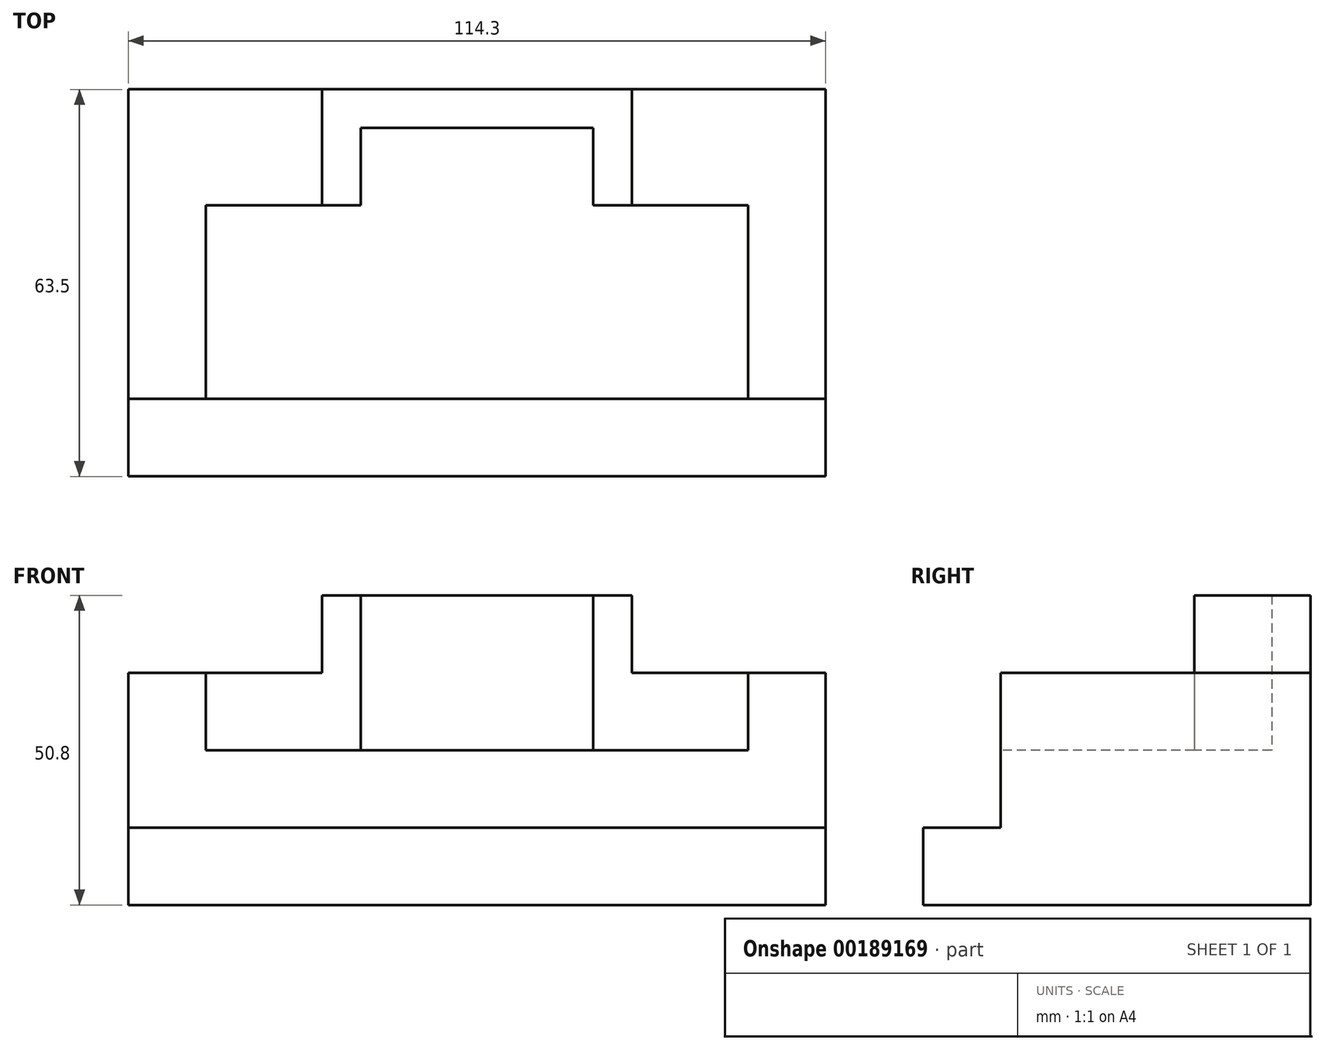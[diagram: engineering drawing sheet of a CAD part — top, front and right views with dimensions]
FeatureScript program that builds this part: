
annotation { "Feature Type Name" : "Feature", "Feature Type Description" : "" }
export const myFeature = defineFeature(function(context is Context, id is Id, definition is map)
    precondition{}
    {
        {
            var Q0;
            Q0=qCreatedBy(makeId("Right.planeOp"),FACE);
            var sketch = newSketch(context, id + "F0", { "sketchPlane" : qUnion([Q0])});
            skLineSegment(sketch, "E0", {"start": v(-32.34, 0) * mm, "end": v(31.16, 0) * mm});
            skLineSegment(sketch, "E1", {"start": v(31.16, 0) * mm, "end": v(31.16, 25.4) * mm});
            skLineSegment(sketch, "E2", {"start": v(31.16, 25.4) * mm, "end": v(-19.64, 25.4) * mm});
            skLineSegment(sketch, "E3", {"start": v(-19.64, 25.4) * mm, "end": v(-19.64, 12.7) * mm});
            skLineSegment(sketch, "E4", {"start": v(-19.64, 12.7) * mm, "end": v(-32.34, 12.7) * mm});
            skLineSegment(sketch, "E5", {"start": v(-32.34, 12.7) * mm, "end": v(-32.34, 0) * mm});
            skSolve(sketch);
        }
        {
            var Q0;
            Q0=makeQuery(id+"F0.imprint","IMPRINT",FACE,{"disambiguationData":[TD([[makeQuery(id+"F0.imprint","IMPRINT",EDGE,{"derivedFrom":sQuery(id+"F0.wireOp",EDGE,"E0")}),1.0]])]});
            extrude(context, id + "F1", {"entities" : qUnion([Q0]), "depth" : 114.3 * mm});
        }
        {
            var Q0;
            Q0=makeQuery(id+"F1.opExtrude","SWEPT_FACE",FACE,{"disambiguationData":[OSD([sQuery(id+"F0.wireOp",EDGE,"E2")])]});
            cPlane(context, id + "F2", {"entities" : qUnion([Q0]), "cplaneType" : CPlaneType.OFFSET, "offset" : 0 * mm, "width" : 152.4 * mm, "height" : 152.4 * mm});
        }
        {
            var Q0;
            Q0=qCreatedBy(id+"F2.planeOp",FACE);
            var sketch = newSketch(context, id + "F3", { "sketchPlane" : qUnion([Q0])});
            skLineSegment(sketch, "E6.0", {"start": v(114.3, 31.16) * mm, "end": v(0, 31.16) * mm});
            skLineSegment(sketch, "E7.0", {"start": v(0, 31.16) * mm, "end": v(0, -19.64) * mm});
            skLineSegment(sketch, "E8.0", {"start": v(114.3, -19.64) * mm, "end": v(0, -19.64) * mm});
            skLineSegment(sketch, "E9.0", {"start": v(114.3, 31.16) * mm, "end": v(114.3, -19.64) * mm});
            skLineSegment(sketch, "E10", {"start": v(0, -19.64) * mm, "end": v(0, 31.16) * mm});
            skLineSegment(sketch, "E11", {"start": v(0, -19.64) * mm, "end": v(12.7, -19.64) * mm});
            skLineSegment(sketch, "E12", {"start": v(12.7, -19.64) * mm, "end": v(12.7, 12.11) * mm});
            skLineSegment(sketch, "E13", {"start": v(12.7, 12.11) * mm, "end": v(38.1, 12.11) * mm});
            skLineSegment(sketch, "E14", {"start": v(38.1, 12.11) * mm, "end": v(38.1, 24.81) * mm});
            skLineSegment(sketch, "E15", {"start": v(38.1, 24.81) * mm, "end": v(76.2, 24.81) * mm});
            skLineSegment(sketch, "E16", {"start": v(76.2, 24.81) * mm, "end": v(76.2, 12.11) * mm});
            skLineSegment(sketch, "E17", {"start": v(76.2, 12.11) * mm, "end": v(101.6, 12.11) * mm});
            skLineSegment(sketch, "E18", {"start": v(101.6, 12.11) * mm, "end": v(101.6, -19.64) * mm});
            skLineSegment(sketch, "E19", {"start": v(101.6, -19.64) * mm, "end": v(114.3, -19.64) * mm});
            skLineSegment(sketch, "E20", {"start": v(114.3, -19.64) * mm, "end": v(114.3, 31.16) * mm});
            skSolve(sketch);
        }
        {
            var Q0;
            Q0=makeQuery(id+"F3.imprint","IMPRINT",FACE,{"disambiguationData":[TD([[makeQuery(id+"F3.imprint","IMPRINT",EDGE,{"derivedFrom":sQuery(id+"F3.wireOp",EDGE,"E6.0")}),1.0]])]});
            extrude(context, id + "F4", {"entities" : qUnion([Q0]), "operationType" : NewBodyOperationType.ADD, "depth" : 12.7 * mm});
        }
        {
            var Q0;
            Q0=makeQuery(id+"F4.opExtrude","CAP_FACE",FACE,{"disambiguationData":[OSD([sQuery(id+"F3.wireOp",EDGE,"E6.0"),sQuery(id+"F3.wireOp",EDGE,"E11"),sQuery(id+"F3.wireOp",EDGE,"E12"),sQuery(id+"F3.wireOp",EDGE,"E13"),sQuery(id+"F3.wireOp",EDGE,"E14"),sQuery(id+"F3.wireOp",EDGE,"E15"),sQuery(id+"F3.wireOp",EDGE,"E16"),sQuery(id+"F3.wireOp",EDGE,"E17"),sQuery(id+"F3.wireOp",EDGE,"E18"),sQuery(id+"F3.wireOp",EDGE,"E19"),sQuery(id+"F3.wireOp",EDGE,"E20"),sQuery(id+"F3.wireOp",EDGE,"E7.0")])],"isStart":false});
            var sketch = newSketch(context, id + "F5", { "sketchPlane" : qUnion([Q0])});
            skLineSegment(sketch, "E21.0.0", {"start": v(114.3, -19.64) * mm, "end": v(114.3, 31.16) * mm});
            skLineSegment(sketch, "E21.0.1", {"start": v(114.3, 31.16) * mm, "end": v(0, 31.16) * mm});
            skLineSegment(sketch, "E21.0.2", {"start": v(0, 31.16) * mm, "end": v(0, -19.64) * mm});
            skLineSegment(sketch, "E21.0.3", {"start": v(0, -19.64) * mm, "end": v(12.7, -19.64) * mm});
            skLineSegment(sketch, "E21.0.4", {"start": v(12.7, -19.64) * mm, "end": v(12.7, 12.11) * mm});
            skLineSegment(sketch, "E21.0.5", {"start": v(12.7, 12.11) * mm, "end": v(38.1, 12.11) * mm});
            skLineSegment(sketch, "E21.0.6", {"start": v(38.1, 12.11) * mm, "end": v(38.1, 24.81) * mm});
            skLineSegment(sketch, "E21.0.7", {"start": v(38.1, 24.81) * mm, "end": v(76.2, 24.81) * mm});
            skLineSegment(sketch, "E21.0.8", {"start": v(76.2, 24.81) * mm, "end": v(76.2, 12.11) * mm});
            skLineSegment(sketch, "E21.0.9", {"start": v(76.2, 12.11) * mm, "end": v(101.6, 12.11) * mm});
            skLineSegment(sketch, "E21.0.10", {"start": v(101.6, 12.11) * mm, "end": v(101.6, -19.64) * mm});
            skLineSegment(sketch, "E21.0.11", {"start": v(101.6, -19.64) * mm, "end": v(114.3, -19.64) * mm});
            skLineSegment(sketch, "E22", {"start": v(31.75, 31.16) * mm, "end": v(31.75, 12.11) * mm});
            skLineSegment(sketch, "E23", {"start": v(31.75, 12.11) * mm, "end": v(38.1, 12.11) * mm});
            skLineSegment(sketch, "E24", {"start": v(76.2, 12.11) * mm, "end": v(82.55, 12.11) * mm});
            skLineSegment(sketch, "E25", {"start": v(82.55, 12.11) * mm, "end": v(82.55, 31.16) * mm});
            skLineSegment(sketch, "E26", {"start": v(82.55, 31.16) * mm, "end": v(31.75, 31.16) * mm});
            skSolve(sketch);
        }
        {
            var Q0;
            Q0=makeQuery(id+"F5.imprint","IMPRINT",FACE,{"disambiguationData":[TD([[makeQuery(id+"F5.imprint","IMPRINT",EDGE,{"derivedFrom":sQuery(id+"F5.wireOp",EDGE,"E21.0.6")}),1.0]])]});
            extrude(context, id + "F6", {"entities" : qUnion([Q0]), "operationType" : NewBodyOperationType.ADD, "depth" : 12.7 * mm});
        }
    });
